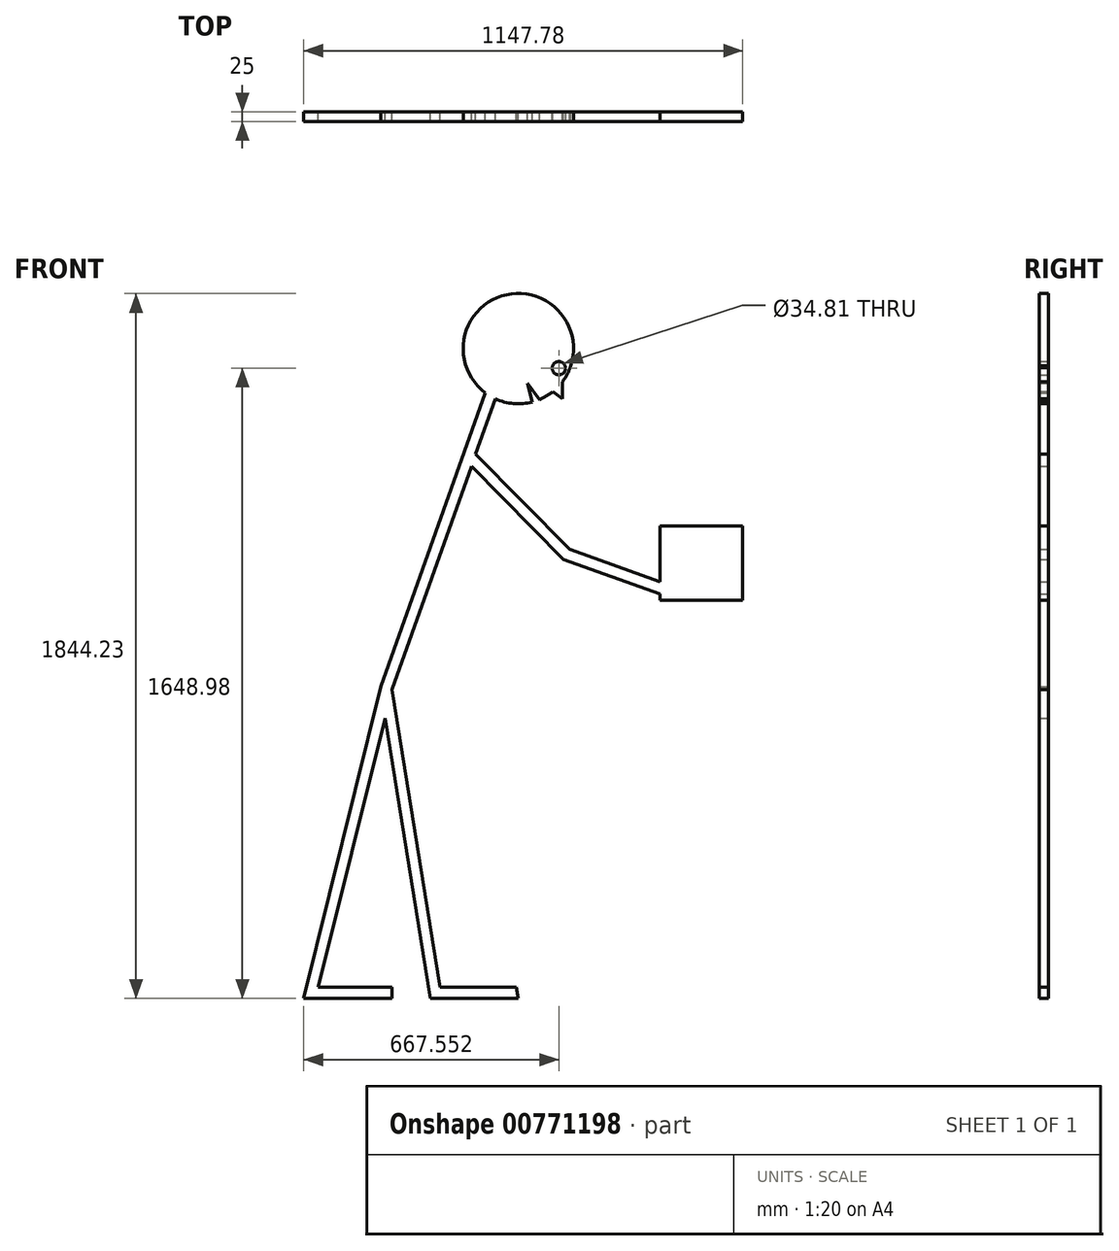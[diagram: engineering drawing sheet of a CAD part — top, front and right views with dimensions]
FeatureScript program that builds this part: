
annotation { "Feature Type Name" : "Feature", "Feature Type Description" : "" }
export const myFeature = defineFeature(function(context is Context, id is Id, definition is map)
    precondition{}
    {
        {
            var Q0;
            Q0=qCreatedBy(makeId("Front.planeOp"),FACE);
            var sketch = newSketch(context, id + "F0", { "sketchPlane" : qUnion([Q0])});
            skArc(sketch, "E0", {"start": v(-60.1, 2143.5) * mm, "mid": v(-12.42, 2130.92) * mm, "end": v(36.71, 2135.13) * mm});
            skLineSegment(sketch, "E1", {"start": v(-60.1, 2143.5) * mm, "end": v(-111.59, 1998.47) * mm});
            skLineSegment(sketch, "E2", {"start": v(-330.37, 1382.26) * mm, "end": v(-204.84, 604.62) * mm});
            skLineSegment(sketch, "E3", {"start": v(-200, 574.62) * mm, "end": v(0, 574.62) * mm});
            skLineSegment(sketch, "E4", {"start": v(-348.76, 1307.97) * mm, "end": v(-522.94, 604.62) * mm});
            skLineSegment(sketch, "E5", {"start": v(-530.37, 574.62) * mm, "end": v(-330.37, 574.62) * mm});
            skLineSegment(sketch, "E6", {"start": v(-111.59, 1998.47) * mm, "end": v(133.78, 1749.44) * mm});
            skLineSegment(sketch, "E7", {"start": v(133.78, 1749.44) * mm, "end": v(370.56, 1665.37) * mm});
            skLineSegment(sketch, "E8", {"start": v(-86.39, 2159.11) * mm, "end": v(-359.13, 1390.9) * mm});
            skLineSegment(sketch, "E9", {"start": v(-359.13, 1390.9) * mm, "end": v(-561.27, 574.62) * mm});
            skLineSegment(sketch, "E10", {"start": v(-561.27, 574.62) * mm, "end": v(-530.37, 574.62) * mm});
            skLineSegment(sketch, "E11", {"start": v(-348.76, 1307.97) * mm, "end": v(-230.39, 574.62) * mm});
            skLineSegment(sketch, "E12", {"start": v(-230.39, 574.62) * mm, "end": v(-200, 574.62) * mm});
            skLineSegment(sketch, "E13", {"start": v(-122.74, 1967.05) * mm, "end": v(117.25, 1723.47) * mm});
            skLineSegment(sketch, "E14", {"start": v(370.56, 1633.54) * mm, "end": v(117.25, 1723.47) * mm});
            skLineSegment(sketch, "E15", {"start": v(-330.37, 574.62) * mm, "end": v(-330.37, 604.62) * mm});
            skLineSegment(sketch, "E16", {"start": v(-330.37, 604.62) * mm, "end": v(-522.94, 604.62) * mm});
            skLineSegment(sketch, "E17", {"start": v(0, 574.62) * mm, "end": v(-4.84, 604.62) * mm});
            skLineSegment(sketch, "E18", {"start": v(-4.84, 604.62) * mm, "end": v(-204.84, 604.62) * mm});
            skLineSegment(sketch, "E19.trimOffspring", {"start": v(-122.74, 1967.05) * mm, "end": v(-330.37, 1382.26) * mm});
            skArc(sketch, "E20.trimOffspring", {"start": v(137.07, 2229.72) * mm, "mid": v(-43.46, 2412.15) * mm, "end": v(-86.39, 2159.11) * mm});
            skLineSegment(sketch, "E21", {"start": v(115.09, 2187.68) * mm, "end": v(115.09, 2143.09) * mm});
            skLineSegment(sketch, "E22", {"start": v(115.09, 2143.09) * mm, "end": v(90.13, 2162) * mm});
            skLineSegment(sketch, "E23", {"start": v(55.48, 2141.48) * mm, "end": v(24.27, 2184.34) * mm});
            skLineSegment(sketch, "E24", {"start": v(24.27, 2184.34) * mm, "end": v(36.71, 2135.13) * mm});
            skArc(sketch, "E25.trimOffspring", {"start": v(115.09, 2187.68) * mm, "mid": v(126.64, 2205.57) * mm, "end": v(135.42, 2224.98) * mm});
            skArc(sketch, "E26.trimOffspring", {"start": v(55.48, 2141.48) * mm, "mid": v(73.53, 2150.53) * mm, "end": v(90.13, 2162) * mm});
            skLineSegment(sketch, "E27", {"start": v(137.07, 2229.72) * mm, "end": v(135.42, 2224.98) * mm});
            skCircle(sketch, "E28", {"center": v(106.28, 2223.6) * mm, "radius": 17.4 * mm});
            skLineSegment(sketch, "E29.bottom", {"start": v(586.5, 1810.65) * mm, "end": v(370.56, 1810.65) * mm});
            skLineSegment(sketch, "E29.top", {"start": v(586.5, 1616.02) * mm, "end": v(370.56, 1616.02) * mm});
            skLineSegment(sketch, "E29.left", {"start": v(586.5, 1810.65) * mm, "end": v(586.5, 1616.02) * mm});
            skLineSegment(sketch, "E29.right", {"start": v(370.56, 1810.65) * mm, "end": v(370.56, 1665.37) * mm});
            skLineSegment(sketch, "E30.trimOffspring", {"start": v(370.56, 1633.54) * mm, "end": v(370.56, 1616.02) * mm});
            skSolve(sketch);
        }
        {
            var Q0;
            Q0=makeQuery(id+"F0.imprint","IMPRINT",FACE,{"disambiguationData":[TD([[makeQuery(id+"F0.imprint","IMPRINT",EDGE,{"derivedFrom":sQuery(id+"F0.wireOp",EDGE,"E0")}),1.0]])]});
            extrude(context, id + "F1", {"entities" : qUnion([Q0]), "depth" : 25 * mm, "offsetDistance" : 25 * mm});
        }
    });
